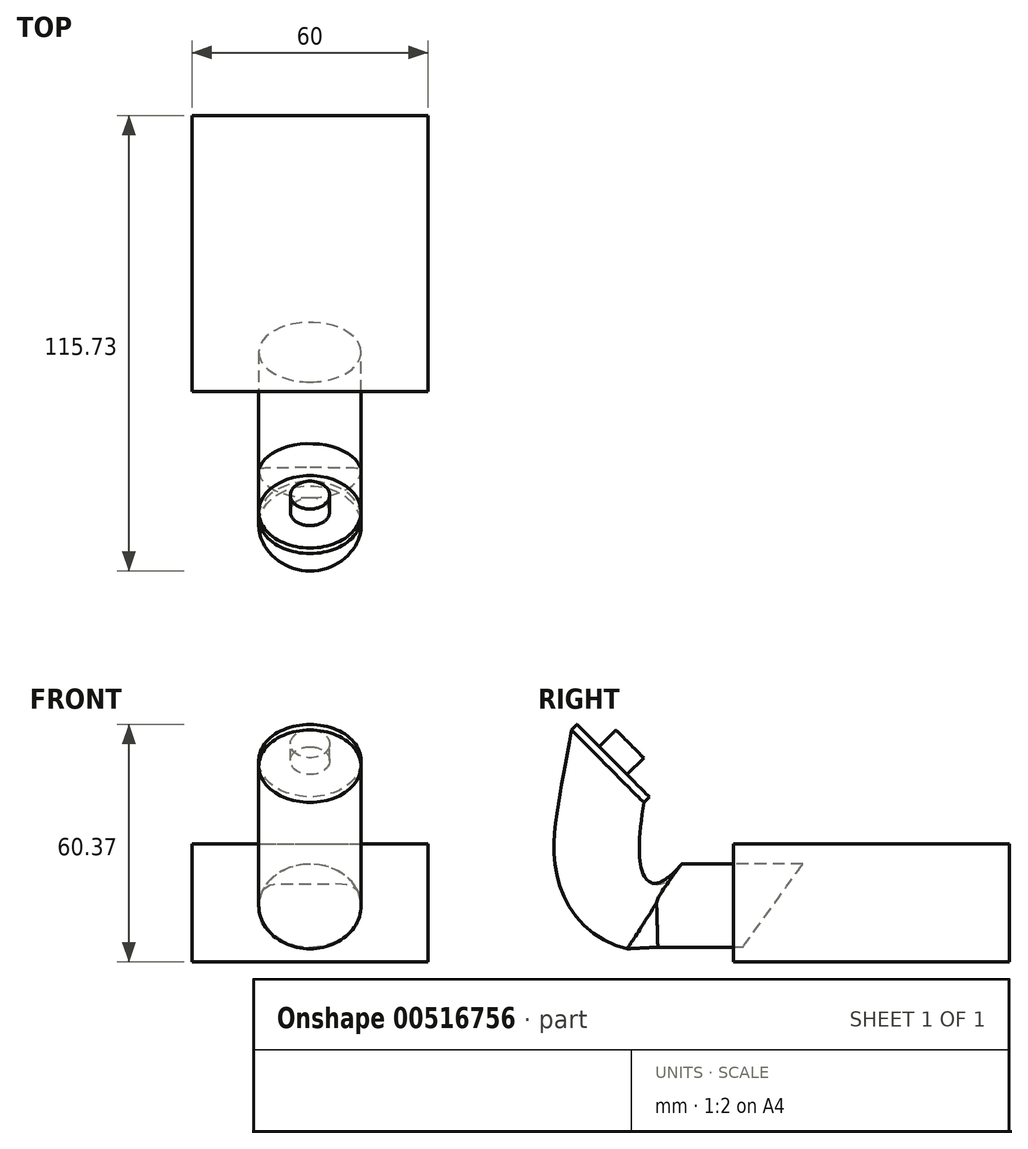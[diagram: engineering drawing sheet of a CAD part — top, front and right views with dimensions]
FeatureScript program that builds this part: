
annotation { "Feature Type Name" : "Feature", "Feature Type Description" : "" }
export const myFeature = defineFeature(function(context is Context, id is Id, definition is map)
    precondition{}
    {
        {
            var Q0;
            Q0=qCreatedBy(makeId("Front.planeOp"),FACE);
            var sketch = newSketch(context, id + "F0", { "sketchPlane" : qUnion([Q0])});
            skLineSegment(sketch, "E0.bottom", {"start": v(50, 12.78) * mm, "end": v(-50, 12.78) * mm});
            skLineSegment(sketch, "E0.top", {"start": v(50, 112.78) * mm, "end": v(-50, 112.78) * mm});
            skLineSegment(sketch, "E0.left", {"start": v(50, 12.78) * mm, "end": v(50, 112.78) * mm});
            skLineSegment(sketch, "E0.right", {"start": v(-50, 12.78) * mm, "end": v(-50, 112.78) * mm});
            skPoint(sketch, "E0.middle", {"position": v(0, 62.78) * mm});
            skSolve(sketch);
        }
        {
            var Q0;
            Q0=qCreatedBy(makeId("Right.planeOp"),FACE);
            var sketch = newSketch(context, id + "F1", { "sketchPlane" : qUnion([Q0])});
            skLineSegment(sketch, "E1", {"start": v(0, 111.74) * mm, "end": v(-100, 111.74) * mm});
            skLineSegment(sketch, "E2", {"start": v(-100, 111.74) * mm, "end": v(-100, 101.74) * mm});
            skLineSegment(sketch, "E3", {"start": v(-100, 101.74) * mm, "end": v(-92.93, 94.67) * mm});
            skSolve(sketch);
        }
        {
            var Q0;
            Q0=sQuery(id+"F1.wireOp",EDGE,"E3");
            cPlane(context, id + "F2", {"entities" : qUnion([Q0]), "cplaneType" : CPlaneType.LINE_ANGLE, "offset" : 25 * mm, "angle" : 0 * degree, "oppositeDirection" : true, "width" : 150 * mm, "height" : 150 * mm});
        }
        {
            var Q0;
            Q0=qCreatedBy(id+"F2.planeOp",FACE);
            var sketch = newSketch(context, id + "F3", { "sketchPlane" : qUnion([Q0])});
            skCircle(sketch, "E4", {"center": v(0, 137.65) * mm, "radius": 5 * mm});
            skSolve(sketch);
        }
        {
            var Q0;
            Q0=makeQuery(id+"F3.imprint","IMPRINT",FACE,{"disambiguationData":[TD([[makeQuery(id+"F3.imprint","IMPRINT",EDGE,{"derivedFrom":sQuery(id+"F3.wireOp",EDGE,"E4")}),1.0]])]});
            extrude(context, id + "F4", {"entities" : qUnion([Q0]), "oppositeDirection" : true, "depth" : 6 * mm, "offsetDistance" : 25 * mm});
        }
        {
            var Q0;
            Q0=makeQuery(id+"F0.imprint","IMPRINT",FACE,{"disambiguationData":[TD([[makeQuery(id+"F0.imprint","IMPRINT",EDGE,{"derivedFrom":sQuery(id+"F0.wireOp",EDGE,"E0.bottom")}),-1.0]])]});
            var sketch = newSketch(context, id + "F5", { "sketchPlane" : qUnion([Q0])});
            skLineSegment(sketch, "E5.bottom", {"start": v(-30, 72.78) * mm, "end": v(30, 72.78) * mm});
            skLineSegment(sketch, "E5.top", {"start": v(-30, 42.78) * mm, "end": v(30, 42.78) * mm});
            skLineSegment(sketch, "E5.left", {"start": v(-30, 72.78) * mm, "end": v(-30, 42.78) * mm});
            skLineSegment(sketch, "E5.right", {"start": v(30, 72.78) * mm, "end": v(30, 42.78) * mm});
            skSolve(sketch);
        }
        {
            var Q0;
            Q0=qCreatedBy(makeId("Right.planeOp"),FACE);
            var sketch = newSketch(context, id + "F6", { "sketchPlane" : qUnion([Q0])});
            skLineSegment(sketch, "E6", {"start": v(0, 62.78) * mm, "end": v(-70.17, 62.78) * mm});
            skSolve(sketch);
        }
        {
            var Q0;
            Q0=makeQuery(id+"F5.imprint","IMPRINT",FACE,{"disambiguationData":[TD([[makeQuery(id+"F5.imprint","IMPRINT",EDGE,{"derivedFrom":sQuery(id+"F5.wireOp",EDGE,"E5.bottom")}),-1.0]])]});
            var Q1;
            Q1=sQuery(id+"F6.wireOp",EDGE,"E6");
            sweep(context, id + "F7", {"operationType" : NewBodyOperationType.ADD, "profiles" : qUnion([Q0]), "path" : qUnion([Q1])});
        }
        {
            var Q0;
            Q0=makeQuery(id+"F7.opSweep","CAP_FACE",FACE,{"disambiguationData":[OSD([sQuery(id+"F5.wireOp",EDGE,"E5.bottom"),sQuery(id+"F5.wireOp",EDGE,"E5.top"),sQuery(id+"F5.wireOp",EDGE,"E5.left"),sQuery(id+"F5.wireOp",EDGE,"E5.right"),sQuery(id+"F6.wireOp",VERTEX,"E6.end")])],"isStart":false});
            var sketch = newSketch(context, id + "F8", { "sketchPlane" : qUnion([Q0])});
            skCircle(sketch, "E7", {"center": v(0, 57.78) * mm, "radius": 13 * mm});
            skSolve(sketch);
        }
        {
            var Q0;
            Q0=qCreatedBy(id+"F2.planeOp",FACE);
            cPlane(context, id + "F9", {"entities" : qUnion([Q0]), "cplaneType" : CPlaneType.OFFSET, "offset" : 6 * mm, "oppositeDirection" : true, "width" : 150 * mm, "height" : 150 * mm});
        }
        {
            var Q0;
            Q0=qCreatedBy(id+"F9.planeOp",FACE);
            var sketch = newSketch(context, id + "F10", { "sketchPlane" : qUnion([Q0])});
            skCircle(sketch, "E8", {"center": v(0, 137.65) * mm, "radius": 13 * mm});
            skSolve(sketch);
        }
        {
            var Q0;
            Q0=makeQuery(id+"F10.imprint","IMPRINT",FACE,{"disambiguationData":[TD([[makeQuery(id+"F10.imprint","IMPRINT",EDGE,{"derivedFrom":sQuery(id+"F10.wireOp",EDGE,"E8")}),1.0]])]});
            extrude(context, id + "F11", {"entities" : qUnion([Q0]), "operationType" : NewBodyOperationType.ADD, "oppositeDirection" : true, "depth" : 2 * mm, "offsetDistance" : 25 * mm});
        }
        {
            var Q0;
            Q0=qCreatedBy(makeId("Right.planeOp"),FACE);
            var sketch = newSketch(context, id + "F12", { "sketchPlane" : qUnion([Q0])});
            skLineSegment(sketch, "E9", {"start": v(-59.66, 57.78) * mm, "end": v(-89.66, 57.78) * mm});
            skFitSpline(sketch, "E10", {"points": [v(-89.66, 57.78) * mm, v(-101.6, 64.3) * mm, v(-101.54, 91.97) * mm], "startDerivative": vector(-42.4, -2.24) * mm, "endDerivative": vector(11.36, 69.44) * mm});
            skSolve(sketch);
        }
        {
            var Q0;
            Q0=makeQuery(id+"F11.opExtrude","CAP_FACE",FACE,{"disambiguationData":[OSD([sQuery(id+"F10.wireOp",EDGE,"E8")])],"isStart":false});
            var Q1;
            Q1=sQuery(id+"F12.wireOp",EDGE,"E10");
            var Q2;
            Q2=sQuery(id+"F12.wireOp",EDGE,"E9");
            sweep(context, id + "F13", {"profiles" : qUnion([Q0]), "path" : qUnion([Q1, Q2])});
        }
    });
